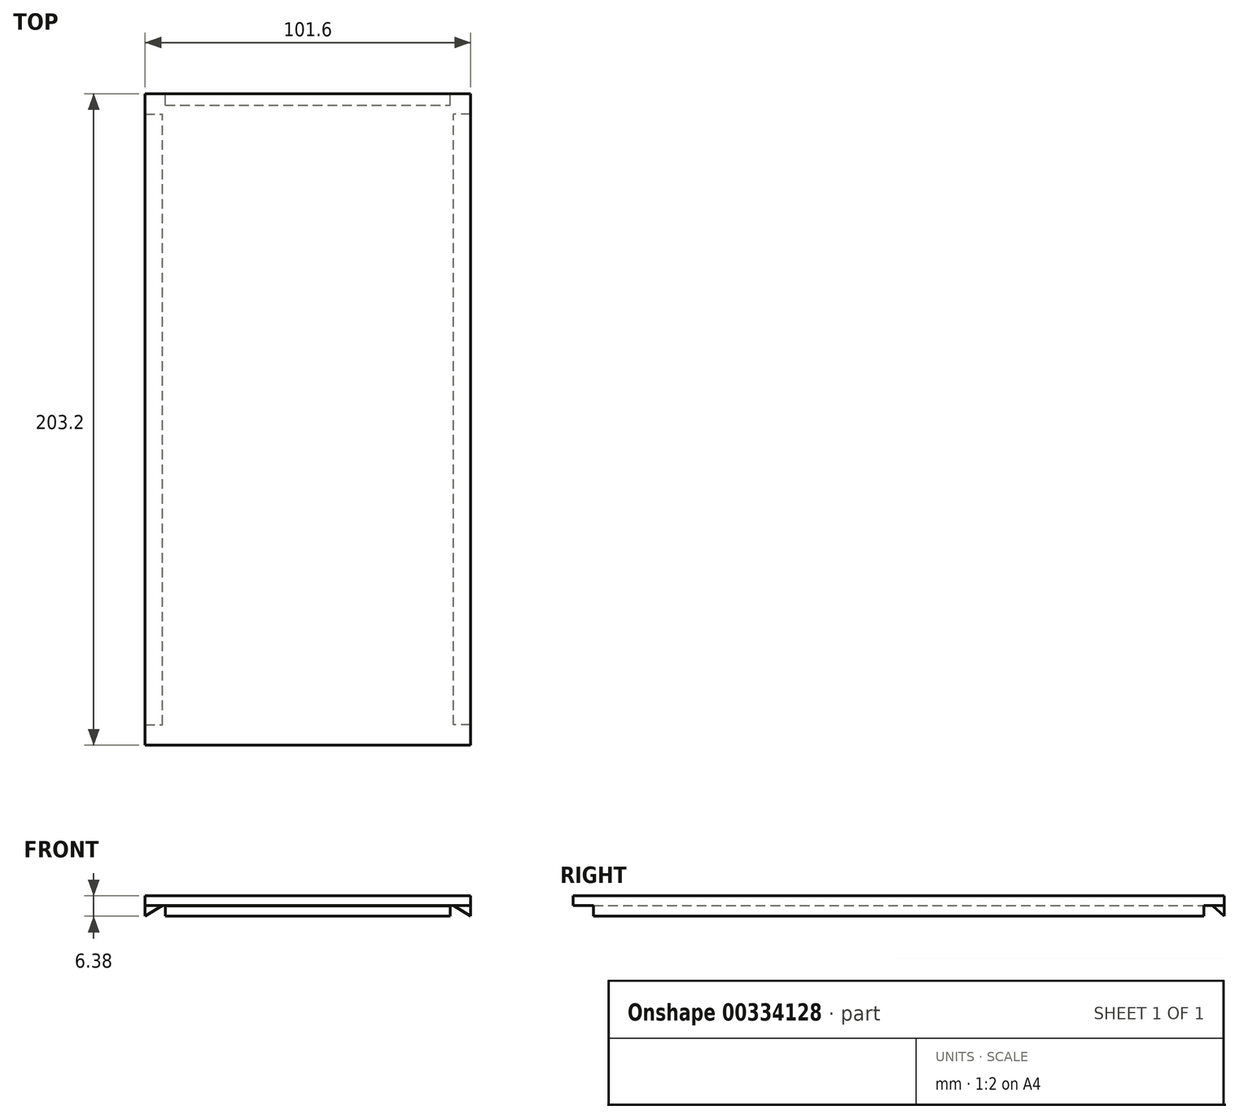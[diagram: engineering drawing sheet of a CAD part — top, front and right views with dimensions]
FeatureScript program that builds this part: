
annotation { "Feature Type Name" : "Feature", "Feature Type Description" : "" }
export const myFeature = defineFeature(function(context is Context, id is Id, definition is map)
    precondition{}
    {
        {
            var Q0;
            Q0=qCreatedBy(makeId("Front.planeOp"),FACE);
            var sketch = newSketch(context, id + "F0", { "sketchPlane" : qUnion([Q0])});
            skLineSegment(sketch, "E0", {"start": v(0, 0) * mm, "end": v(50.8, 0) * mm});
            skLineSegment(sketch, "E1", {"start": v(0, 0) * mm, "end": v(-50.8, 0) * mm});
            skLineSegment(sketch, "E2", {"start": v(-50.8, 0) * mm, "end": v(-50.8, -6.35) * mm});
            skLineSegment(sketch, "E3", {"start": v(50.8, 0) * mm, "end": v(50.8, -6.35) * mm});
            skLineSegment(sketch, "E4", {"start": v(-50.8, -6.35) * mm, "end": v(-45.39, -3.03) * mm});
            skLineSegment(sketch, "E5", {"start": v(50.8, -6.35) * mm, "end": v(45.38, -3.03) * mm});
            skLineSegment(sketch, "E6", {"start": v(-45.39, -3.03) * mm, "end": v(45.38, -3.03) * mm});
            skSolve(sketch);
        }
        {
            var Q0;
            Q0=makeQuery(id+"F0.imprint","IMPRINT",FACE,{"disambiguationData":[TD([[makeQuery(id+"F0.imprint","IMPRINT",EDGE,{"derivedFrom":sQuery(id+"F0.wireOp",EDGE,"E0")}),-1.0]])]});
            extrude(context, id + "F1", {"entities" : qUnion([Q0]), "depth" : 203.2 * mm});
        }
        {
            var Q0;
            Q0=qCreatedBy(makeId("Right.planeOp"),FACE);
            var sketch = newSketch(context, id + "F2", { "sketchPlane" : qUnion([Q0])});
            skLineSegment(sketch, "E7", {"start": v(0, 0) * mm, "end": v(0, -6.38) * mm});
            skLineSegment(sketch, "E8", {"start": v(0, -6.38) * mm, "end": v(-3.55, -3.15) * mm});
            skLineSegment(sketch, "E9", {"start": v(-3.55, -3.15) * mm, "end": v(-3.55, 0) * mm});
            skLineSegment(sketch, "E10", {"start": v(0, 0) * mm, "end": v(-3.55, 0) * mm});
            skSolve(sketch);
        }
        {
            var Q0;
            Q0 = qSketchRegion(id + "F2", true);
            extrude(context, id + "F3", {"entities" : qUnion([Q0]), "operationType" : NewBodyOperationType.ADD, "endBound" : BoundingType.SYMMETRIC, "depth" : 88.9 * mm});
        }
        {
            var Q0;
            Q0=qCreatedBy(makeId("Front.planeOp"),FACE);
            var sketch = newSketch(context, id + "F4", { "sketchPlane" : qUnion([Q0])});
            skLineSegment(sketch, "E11", {"start": v(45.38, -3.03) * mm, "end": v(50.8, -3.03) * mm});
            skLineSegment(sketch, "E12", {"start": v(50.8, -3.03) * mm, "end": v(50.8, -6.35) * mm});
            skLineSegment(sketch, "E13", {"start": v(50.8, -6.35) * mm, "end": v(45.38, -3.03) * mm});
            skLineSegment(sketch, "E14.MirrorCS", {"start": v(-50.8, -6.35) * mm, "end": v(-45.38, -3.03) * mm});
            skLineSegment(sketch, "E15.MirrorCS", {"start": v(-45.38, -3.03) * mm, "end": v(-50.8, -3.03) * mm});
            skLineSegment(sketch, "E16.MirrorCS", {"start": v(-50.8, -3.03) * mm, "end": v(-50.8, -6.35) * mm});
            skSolve(sketch);
        }
        {
            var Q0;
            Q0=makeQuery(id+"F4.imprint","IMPRINT",FACE,{"disambiguationData":[TD([[makeQuery(id+"F4.imprint","IMPRINT",EDGE,{"derivedFrom":sQuery(id+"F4.wireOp",EDGE,"E11")}),-1.0]])]});
            var Q1;
            Q1=makeQuery(id+"F4.imprint","IMPRINT",FACE,{"disambiguationData":[TD([[makeQuery(id+"F4.imprint","IMPRINT",EDGE,{"derivedFrom":sQuery(id+"F4.wireOp",EDGE,"E15.MirrorCS")}),1.0]])]});
            extrude(context, id + "F5", {"entities" : qUnion([Q0, Q1]), "operationType" : NewBodyOperationType.REMOVE, "depth" : 6.35 * mm});
        }
        {
            var Q0;
            Q0=makeQuery(id+"F1.opExtrude","CAP_FACE",FACE,{"disambiguationData":[OSD([sQuery(id+"F0.wireOp",EDGE,"E0"),sQuery(id+"F0.wireOp",EDGE,"E1"),sQuery(id+"F0.wireOp",EDGE,"E2"),sQuery(id+"F0.wireOp",EDGE,"E3"),sQuery(id+"F0.wireOp",EDGE,"E4"),sQuery(id+"F0.wireOp",EDGE,"E5"),sQuery(id+"F0.wireOp",EDGE,"E6")])],"isStart":false});
            var sketch = newSketch(context, id + "F6", { "sketchPlane" : qUnion([Q0])});
            skLineSegment(sketch, "E17", {"start": v(-45.39, -3.03) * mm, "end": v(-50.8, -3.03) * mm});
            skLineSegment(sketch, "E18", {"start": v(-50.8, -3.03) * mm, "end": v(-50.8, -6.35) * mm});
            skLineSegment(sketch, "E19", {"start": v(-50.8, -6.35) * mm, "end": v(-45.39, -3.03) * mm});
            skLineSegment(sketch, "E20", {"start": v(45.38, -3.03) * mm, "end": v(50.8, -3.03) * mm});
            skLineSegment(sketch, "E21", {"start": v(50.8, -3.03) * mm, "end": v(50.8, -6.35) * mm});
            skLineSegment(sketch, "E22", {"start": v(50.8, -6.35) * mm, "end": v(45.38, -3.03) * mm});
            skSolve(sketch);
        }
        {
            var Q0;
            Q0=makeQuery(id+"F6.imprint","IMPRINT",FACE,{"disambiguationData":[TD([[makeQuery(id+"F6.imprint","IMPRINT",EDGE,{"derivedFrom":sQuery(id+"F6.wireOp",EDGE,"E17")}),1.0]])]});
            var Q1;
            Q1=makeQuery(id+"F6.imprint","IMPRINT",FACE,{"disambiguationData":[TD([[makeQuery(id+"F6.imprint","IMPRINT",EDGE,{"derivedFrom":sQuery(id+"F6.wireOp",EDGE,"E20")}),-1.0]])]});
            extrude(context, id + "F7", {"entities" : qUnion([Q0, Q1]), "operationType" : NewBodyOperationType.REMOVE, "oppositeDirection" : true, "depth" : 6.35 * mm});
        }
        {
            var Q0;
            Q0=qCreatedBy(makeId("Front.planeOp"),FACE);
            cPlane(context, id + "F8", {"entities" : qUnion([Q0]), "cplaneType" : CPlaneType.OFFSET, "offset" : 101.6 * mm, "width" : 152.4 * mm, "height" : 152.4 * mm});
        }
    });
